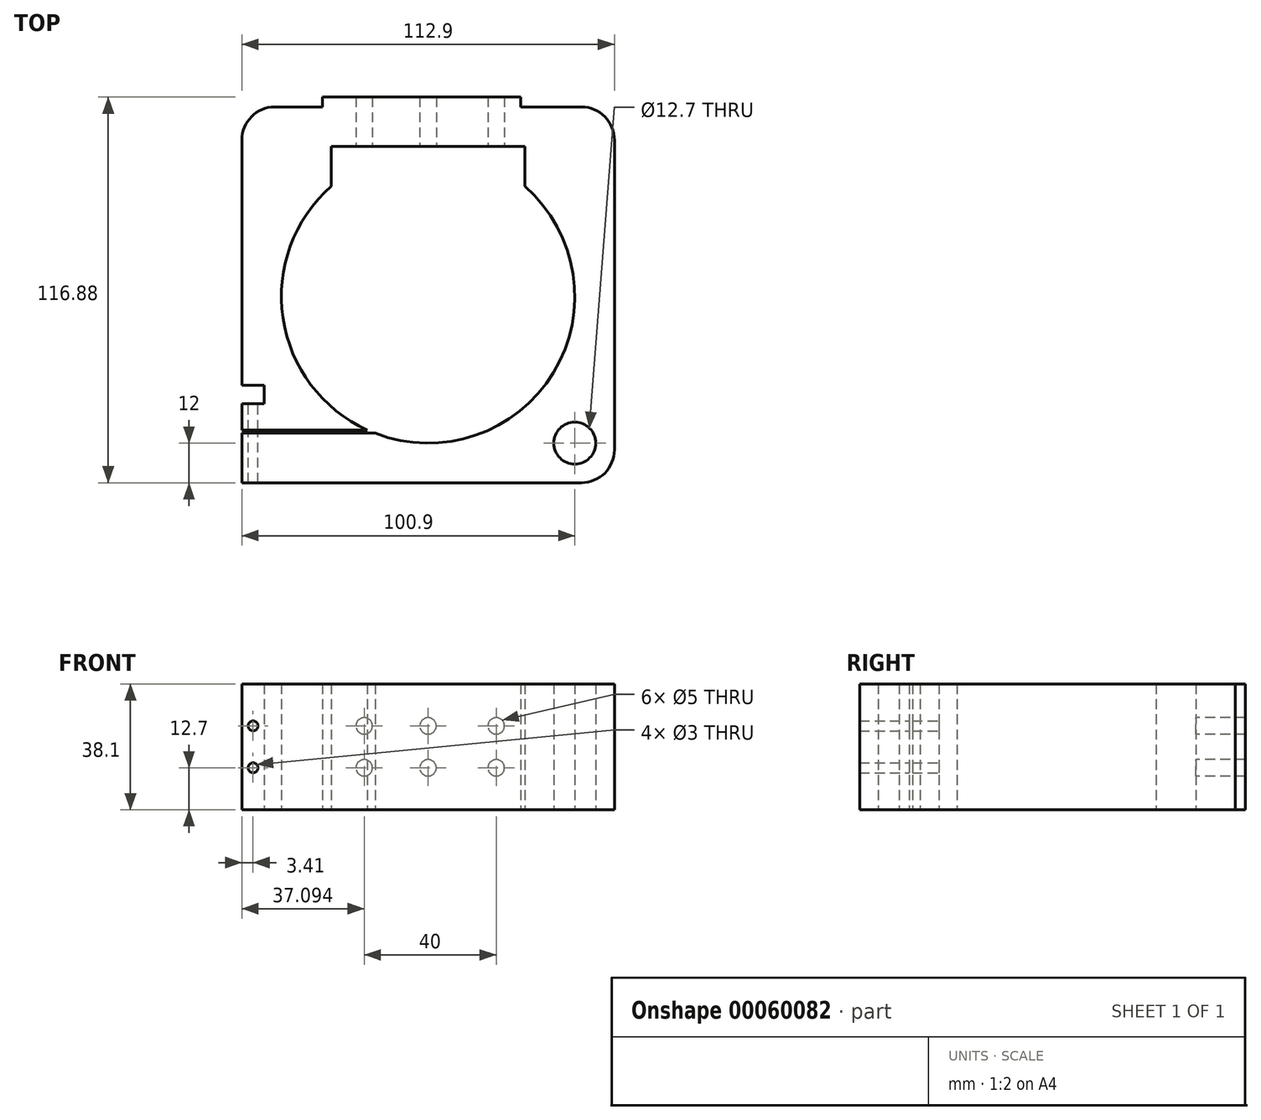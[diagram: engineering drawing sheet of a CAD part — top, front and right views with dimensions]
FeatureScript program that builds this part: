
annotation { "Feature Type Name" : "Feature", "Feature Type Description" : "" }
export const myFeature = defineFeature(function(context is Context, id is Id, definition is map)
    precondition{}
    {
        {
            var Q0;
            Q0=qCreatedBy(makeId("Top.planeOp"),FACE);
            var sketch = newSketch(context, id + "F0", { "sketchPlane" : qUnion([Q0])});
            skArc(sketch, "E0", {"start": v(-29.36, 33.38) * mm, "mid": v(-43.97, -6.5) * mm, "end": v(-18.43, -40.45) * mm});
            skLineSegment(sketch, "E1.bottom", {"start": v(-56.45, 57.43) * mm, "end": v(-32, 57.43) * mm});
            skLineSegment(sketch, "E1.top", {"start": v(-56.45, -56.45) * mm, "end": v(56.45, -56.45) * mm});
            skLineSegment(sketch, "E1.left", {"start": v(-56.45, 57.43) * mm, "end": v(-56.45, -26.95) * mm});
            skLineSegment(sketch, "E1.right", {"start": v(56.45, 57.43) * mm, "end": v(56.45, -56.45) * mm});
            skLineSegment(sketch, "E2", {"start": v(-56.45, 0) * mm, "end": v(-44.45, 0) * mm, "construction": true});
            skLineSegment(sketch, "E3", {"start": v(44.45, 0) * mm, "end": v(56.45, 0) * mm, "construction": true});
            skLineSegment(sketch, "E4", {"start": v(0, -44.45) * mm, "end": v(0, -56.45) * mm, "construction": true});
            skLineSegment(sketch, "E5.bottom", {"start": v(-29.36, 45.43) * mm, "end": v(29.36, 45.43) * mm});
            skLineSegment(sketch, "E5.left", {"start": v(-29.36, 45.43) * mm, "end": v(-29.36, 33.38) * mm});
            skLineSegment(sketch, "E5.right", {"start": v(29.36, 45.43) * mm, "end": v(29.36, 33.38) * mm});
            skPoint(sketch, "E6.visualSharp", {"position": v(56.45, -56.45) * mm});
            skLineSegment(sketch, "E7", {"start": v(-56.45, -41.45) * mm, "end": v(-16.05, -41.45) * mm});
            skLineSegment(sketch, "E8", {"start": v(-56.45, -40.45) * mm, "end": v(-18.43, -40.45) * mm});
            skLineSegment(sketch, "E9", {"start": v(-57.27, -40.45) * mm, "end": v(-57.27, -41.45) * mm, "construction": true});
            skLineSegment(sketch, "E10", {"start": v(-57.27, -41.45) * mm, "end": v(-57.27, -56.45) * mm, "construction": true});
            skLineSegment(sketch, "E11.top", {"start": v(-32, 60.43) * mm, "end": v(28, 60.43) * mm});
            skLineSegment(sketch, "E11.left", {"start": v(-32, 57.43) * mm, "end": v(-32, 60.43) * mm});
            skLineSegment(sketch, "E11.right", {"start": v(28, 57.43) * mm, "end": v(28, 60.43) * mm});
            skLineSegment(sketch, "E12", {"start": v(-32, 57.43) * mm, "end": v(-32, 45.43) * mm, "construction": true});
            skLineSegment(sketch, "E13", {"start": v(-32, 45.43) * mm, "end": v(-29.36, 45.43) * mm, "construction": true});
            skLineSegment(sketch, "E14.bottom", {"start": v(-56.45, -32.45) * mm, "end": v(-49.63, -32.45) * mm});
            skLineSegment(sketch, "E14.right", {"start": v(-49.63, -32.45) * mm, "end": v(-49.63, -26.95) * mm});
            skLineSegment(sketch, "E15", {"start": v(-49.63, -32.45) * mm, "end": v(-49.63, -40.45) * mm, "construction": true});
            skLineSegment(sketch, "E16", {"start": v(-49.63, -26.95) * mm, "end": v(-39.26, -20.91) * mm, "construction": true});
            skLineSegment(sketch, "E17", {"start": v(-39.26, -20.91) * mm, "end": v(-31.1, -34.93) * mm, "construction": true});
            skLineSegment(sketch, "E18", {"start": v(44.45, -56.45) * mm, "end": v(44.45, -44.45) * mm, "construction": true});
            skLineSegment(sketch, "E19", {"start": v(44.45, -44.45) * mm, "end": v(56.45, -44.45) * mm, "construction": true});
            skCircle(sketch, "E20", {"center": v(44.45, -44.45) * mm, "radius": 6.35 * mm});
            skArc(sketch, "E21.trimOffspring", {"start": v(-16.05, -41.45) * mm, "mid": v(38, -23.06) * mm, "end": v(29.36, 33.38) * mm});
            skLineSegment(sketch, "E22.trimOffspring", {"start": v(-56.45, -41.45) * mm, "end": v(-56.45, -56.45) * mm});
            skLineSegment(sketch, "E23.trimOffspring", {"start": v(28, 57.43) * mm, "end": v(56.45, 57.43) * mm});
            skLineSegment(sketch, "E24", {"start": v(-49.63, -26.95) * mm, "end": v(-56.45, -26.95) * mm});
            skLineSegment(sketch, "E25.trimOffspring", {"start": v(-56.45, -32.45) * mm, "end": v(-56.45, -40.45) * mm});
            skSolve(sketch);
        }
        {
            var Q0;
            Q0=makeQuery(id+"F0.imprint","IMPRINT",FACE,{"disambiguationData":[TD([[makeQuery(id+"F0.imprint","IMPRINT",EDGE,{"derivedFrom":sQuery(id+"F0.wireOp",EDGE,"E0")}),-1.0]])]});
            extrude(context, id + "F1", {"entities" : qUnion([Q0]), "depth" : 38.1 * mm});
        }
        {
            var Q0;
            Q0=makeQuery(id+"F1.opExtrude","SWEPT_FACE",FACE,{"disambiguationData":[OSD([sQuery(id+"F0.wireOp",EDGE,"E5.bottom")])]});
            var sketch = newSketch(context, id + "F2", { "sketchPlane" : qUnion([Q0])});
            skLineSegment(sketch, "E26", {"start": v(-19.36, 12.7) * mm, "end": v(-29.36, 12.7) * mm, "construction": true});
            skPoint(sketch, "E26.endSnap0", {"position": v(-29.36, 19.05) * mm});
            skLineSegment(sketch, "E27", {"start": v(-19.36, 12.7) * mm, "end": v(20.64, 12.7) * mm, "construction": true});
            skLineSegment(sketch, "E28", {"start": v(-19.36, 12.7) * mm, "end": v(-19.36, 0) * mm, "construction": true});
            skLineSegment(sketch, "E29", {"start": v(-19.36, 12.7) * mm, "end": v(-19.36, 25.4) * mm, "construction": true});
            skLineSegment(sketch, "E30", {"start": v(-19.36, 25.4) * mm, "end": v(20.64, 25.4) * mm, "construction": true});
            skPoint(sketch, "E31", {"position": v(0, 25.4) * mm});
            skPoint(sketch, "E32", {"position": v(0, 12.7) * mm});
            skSolve(sketch);
        }
        {
            var Q0;
            Q0=sQuery(id+"F2.wireOp",VERTEX,"E30.start");
            var Q1;
            Q1=sQuery(id+"F2.wireOp",VERTEX,"E29.start");
            var Q2;
            Q2=sQuery(id+"F2.wireOp",VERTEX,"E30.end");
            var Q3;
            Q3=sQuery(id+"F2.wireOp",VERTEX,"E27.end");
            var Q4;
            Q4=sQuery(id+"F2.wireOp",VERTEX,"E31");
            var Q5;
            Q5=sQuery(id+"F2.wireOp",VERTEX,"E32");
            var Q6;
            Q6=makeQuery(id+"F1.opExtrude","SWEPT_BODY",BODY,{"disambiguationData":[OSD([sQuery(id+"F0.wireOp",EDGE,"E0"),sQuery(id+"F0.wireOp",EDGE,"E1.bottom"),sQuery(id+"F0.wireOp",EDGE,"E1.top"),sQuery(id+"F0.wireOp",EDGE,"E1.left"),sQuery(id+"F0.wireOp",EDGE,"E1.right"),sQuery(id+"F0.wireOp",EDGE,"E5.bottom"),sQuery(id+"F0.wireOp",EDGE,"E5.left"),sQuery(id+"F0.wireOp",EDGE,"E5.right"),sQuery(id+"F0.wireOp",EDGE,"E6.filletArc"),sQuery(id+"F0.wireOp",EDGE,"E7"),sQuery(id+"F0.wireOp",EDGE,"E8"),sQuery(id+"F0.wireOp",EDGE,"E11.top"),sQuery(id+"F0.wireOp",EDGE,"E11.left"),sQuery(id+"F0.wireOp",EDGE,"E11.right"),sQuery(id+"F0.wireOp",EDGE,"E14.bottom"),sQuery(id+"F0.wireOp",EDGE,"E14.top"),sQuery(id+"F0.wireOp",EDGE,"E14.right"),sQuery(id+"F0.wireOp",EDGE,"E20"),sQuery(id+"F0.wireOp",EDGE,"E21.trimOffspring"),sQuery(id+"F0.wireOp",EDGE,"E22.trimOffspring"),sQuery(id+"F0.wireOp",EDGE,"E23.trimOffspring")])]});
            hole(context, id + "F3", {"style" : HoleStyle.SIMPLE, "holeDiameter" : 5 * mm, "endStyle" : HoleEndStyle.THROUGH, "locations" : qUnion([Q0, Q1, Q2, Q3, Q4, Q5]), "scope" : qUnion([Q6])});
        }
        {
            var Q0;
            Q0=makeQuery(id+"F1.opExtrude","SWEPT_FACE",FACE,{"disambiguationData":[OSD([sQuery(id+"F0.wireOp",EDGE,"E24")])]});
            var sketch = newSketch(context, id + "F4", { "sketchPlane" : qUnion([Q0])});
            skLineSegment(sketch, "E33", {"start": v(-53.04, 38.1) * mm, "end": v(-53.04, 25.4) * mm, "construction": true});
            skLineSegment(sketch, "E34", {"start": v(-53.04, 25.4) * mm, "end": v(-53.04, 12.7) * mm, "construction": true});
            skSolve(sketch);
        }
        {
            var Q0;
            Q0=sQuery(id+"F4.wireOp",VERTEX,"E33.end");
            var Q1;
            Q1=sQuery(id+"F4.wireOp",VERTEX,"E34.end");
            var Q2;
            Q2=makeQuery(id+"F1.opExtrude","SWEPT_BODY",BODY,{"disambiguationData":[OSD([sQuery(id+"F0.wireOp",EDGE,"E0"),sQuery(id+"F0.wireOp",EDGE,"E1.bottom"),sQuery(id+"F0.wireOp",EDGE,"E1.top"),sQuery(id+"F0.wireOp",EDGE,"E1.left"),sQuery(id+"F0.wireOp",EDGE,"E1.right"),sQuery(id+"F0.wireOp",EDGE,"E5.bottom"),sQuery(id+"F0.wireOp",EDGE,"E5.left"),sQuery(id+"F0.wireOp",EDGE,"E5.right"),sQuery(id+"F0.wireOp",EDGE,"E6.filletArc"),sQuery(id+"F0.wireOp",EDGE,"E7"),sQuery(id+"F0.wireOp",EDGE,"E8"),sQuery(id+"F0.wireOp",EDGE,"E11.top"),sQuery(id+"F0.wireOp",EDGE,"E11.left"),sQuery(id+"F0.wireOp",EDGE,"E11.right"),sQuery(id+"F0.wireOp",EDGE,"E14.bottom"),sQuery(id+"F0.wireOp",EDGE,"E14.top"),sQuery(id+"F0.wireOp",EDGE,"E14.right"),sQuery(id+"F0.wireOp",EDGE,"E20"),sQuery(id+"F0.wireOp",EDGE,"E21.trimOffspring"),sQuery(id+"F0.wireOp",EDGE,"E22.trimOffspring"),sQuery(id+"F0.wireOp",EDGE,"E23.trimOffspring")])]});
            hole(context, id + "F5", {"style" : HoleStyle.SIMPLE, "holeDiameter" : 3 * mm, "endStyle" : HoleEndStyle.THROUGH, "oppositeDirection" : true, "locations" : qUnion([Q0, Q1]), "scope" : qUnion([Q2])});
        }
        {
            var Q0;
            Q0=makeQuery(id+"F1.opExtrude","SWEPT_EDGE",EDGE,{"disambiguationData":[OSD([sQuery(id+"F0.wireOp",EDGE,"E1.right"),sQuery(id+"F0.wireOp",EDGE,"E23.trimOffspring")])]});
            var Q1;
            Q1=makeQuery(id+"F1.opExtrude","SWEPT_EDGE",EDGE,{"disambiguationData":[OSD([sQuery(id+"F0.wireOp",EDGE,"E1.bottom"),sQuery(id+"F0.wireOp",EDGE,"E1.left")])]});
            var Q2;
            Q2=makeQuery(id+"F1.opExtrude","SWEPT_EDGE",EDGE,{"disambiguationData":[OSD([sQuery(id+"F0.wireOp",EDGE,"E1.top"),sQuery(id+"F0.wireOp",EDGE,"E1.right")])]});
            fillet(context, id + "F6", {"entities" : qUnion([Q0, Q1, Q2]), "radius" : 10 * mm, "tangentPropagation" : true, "allowEdgeOverflow" : false});
        }
    });
